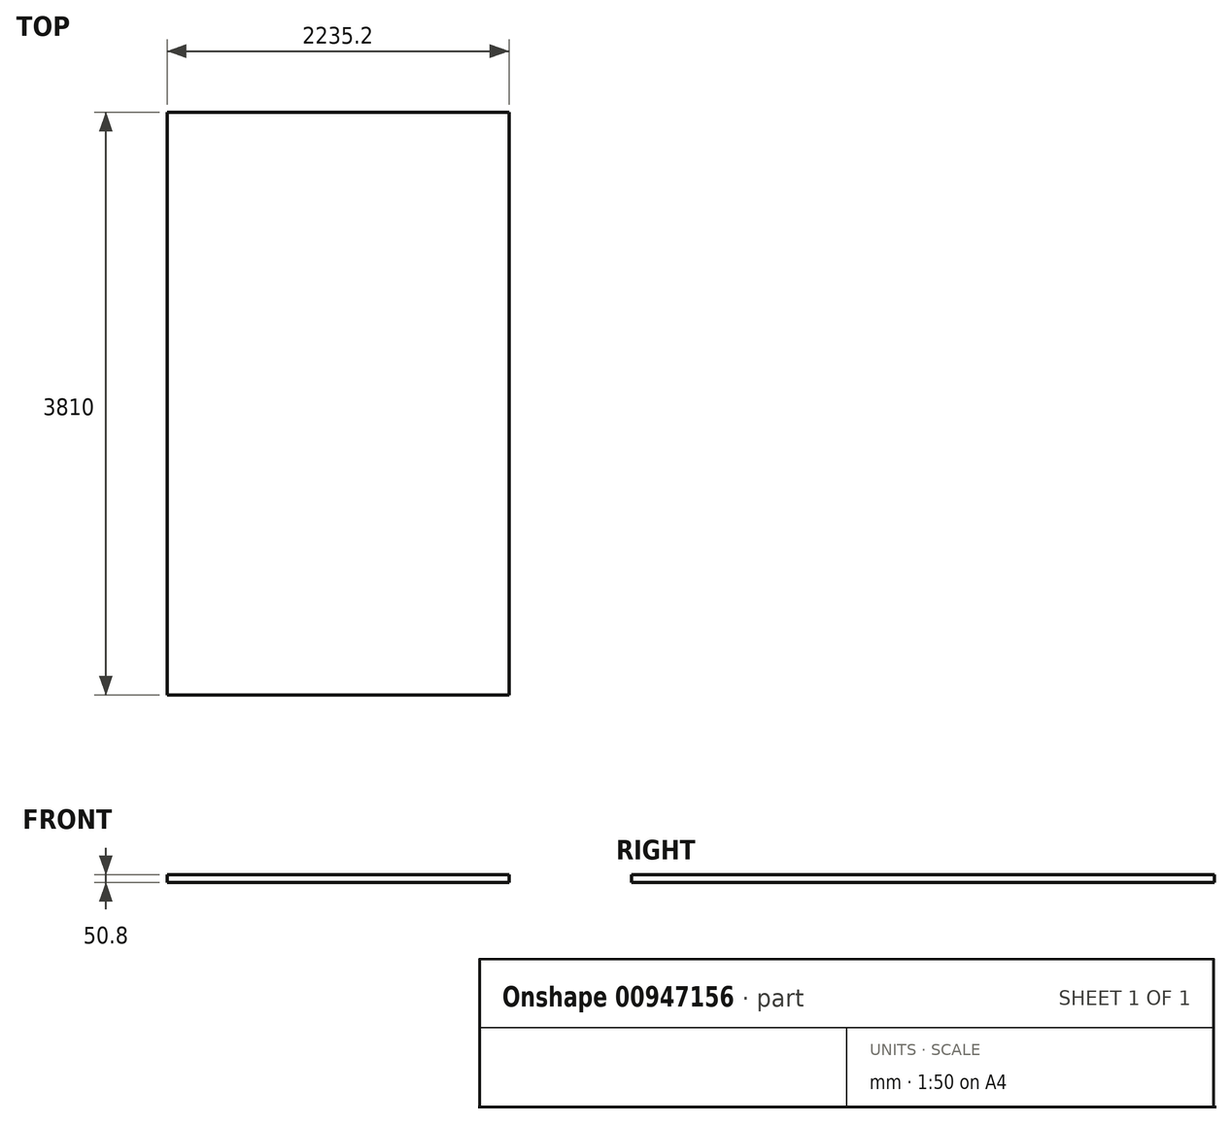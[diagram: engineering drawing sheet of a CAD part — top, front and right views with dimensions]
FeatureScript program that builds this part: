
annotation { "Feature Type Name" : "Feature", "Feature Type Description" : "" }
export const myFeature = defineFeature(function(context is Context, id is Id, definition is map)
    precondition{}
    {
        {
            var Q0;
            Q0=qCreatedBy(makeId("Top.planeOp"),FACE);
            var sketch = newSketch(context, id + "F0", { "sketchPlane" : qUnion([Q0])});
            skLineSegment(sketch, "E0.bottom", {"start": v(3.2, 3810) * mm, "end": v(2238.4, 3810) * mm});
            skLineSegment(sketch, "E0.top", {"start": v(3.2, 0) * mm, "end": v(2238.4, 0) * mm});
            skLineSegment(sketch, "E0.left", {"start": v(3.2, 3810) * mm, "end": v(3.2, 0) * mm});
            skLineSegment(sketch, "E0.right", {"start": v(2238.4, 3810) * mm, "end": v(2238.4, 0) * mm});
            skSolve(sketch);
        }
        {
            var Q0;
            Q0 = qSketchRegion(id + "F0", true);
            extrude(context, id + "F1", {"entities" : qUnion([Q0]), "depth" : 50.8 * mm, "offsetDistance" : 25.4 * mm});
        }
    });
